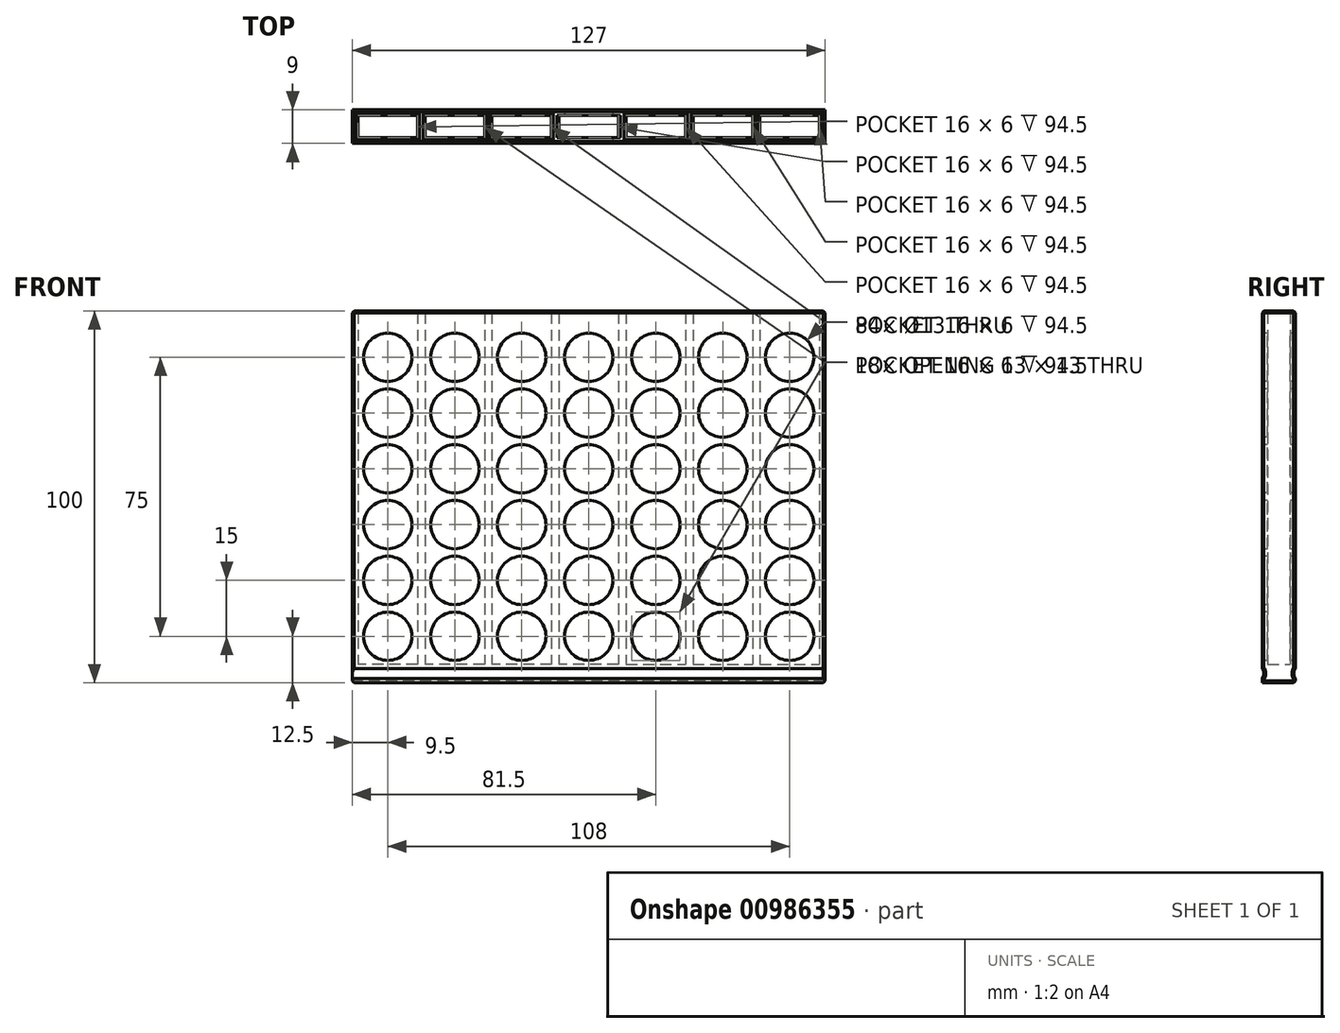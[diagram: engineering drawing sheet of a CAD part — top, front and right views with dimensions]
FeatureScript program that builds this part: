
annotation { "Feature Type Name" : "Feature", "Feature Type Description" : "" }
export const myFeature = defineFeature(function(context is Context, id is Id, definition is map)
    precondition{}
    {
        {
            var Q0;
            Q0=qCreatedBy(makeId("Top.planeOp"),FACE);
            var sketch = newSketch(context, id + "F0", { "sketchPlane" : qUnion([Q0])});
            skLineSegment(sketch, "E0.bottom", {"start": v(63.5, -4.5) * mm, "end": v(-26, -4.5) * mm});
            skLineSegment(sketch, "E0.top", {"start": v(63.5, 4.5) * mm, "end": v(-63.5, 4.5) * mm});
            skLineSegment(sketch, "E0.left", {"start": v(63.5, -4.5) * mm, "end": v(63.5, 4.5) * mm});
            skLineSegment(sketch, "E0.right", {"start": v(-63.5, -4.5) * mm, "end": v(-63.5, 4.5) * mm});
            skPoint(sketch, "E0.middle", {"position": v(0, 0) * mm});
            skLineSegment(sketch, "E1.0", {"start": v(8, 3) * mm, "end": v(-8, 3) * mm});
            skLineSegment(sketch, "E1.1", {"start": v(62, -3) * mm, "end": v(62, 3) * mm});
            skLineSegment(sketch, "E1.2", {"start": v(8, -3) * mm, "end": v(-8, -3) * mm});
            skLineSegment(sketch, "E1.3", {"start": v(-62, -3) * mm, "end": v(-62, 3) * mm});
            skLineSegment(sketch, "E2.left", {"start": v(8, -3) * mm, "end": v(8, 3) * mm, "construction": true});
            skLineSegment(sketch, "E2.right", {"start": v(-8, -3) * mm, "end": v(-8, 3) * mm, "construction": true});
            skLineSegment(sketch, "E3.top", {"start": v(-8, -4.5) * mm, "end": v(-10, -4.5) * mm});
            skLineSegment(sketch, "E3.left", {"start": v(-8, 3) * mm, "end": v(-8, -3) * mm});
            skLineSegment(sketch, "E3.right", {"start": v(-10, 3) * mm, "end": v(-10, -3) * mm});
            skLineSegment(sketch, "E4.top", {"start": v(-10, 4.5) * mm, "end": v(-26, 4.5) * mm, "construction": true});
            skLineSegment(sketch, "E4.left", {"start": v(-10, -3) * mm, "end": v(-10, 3) * mm, "construction": true});
            skLineSegment(sketch, "E4.right", {"start": v(-26, -3) * mm, "end": v(-26, 3) * mm, "construction": true});
            skLineSegment(sketch, "E5.bottom", {"start": v(-26, -4.5) * mm, "end": v(-28, -4.5) * mm});
            skLineSegment(sketch, "E5.top", {"start": v(-26, 4.5) * mm, "end": v(-28, 4.5) * mm});
            skLineSegment(sketch, "E5.left", {"start": v(-26, -3) * mm, "end": v(-26, 3) * mm});
            skLineSegment(sketch, "E5.right", {"start": v(-28, -3) * mm, "end": v(-28, 3) * mm});
            skLineSegment(sketch, "E6.top", {"start": v(-28, 4.5) * mm, "end": v(-44, 4.5) * mm, "construction": true});
            skLineSegment(sketch, "E6.left", {"start": v(-28, -3) * mm, "end": v(-28, 3) * mm, "construction": true});
            skLineSegment(sketch, "E6.right", {"start": v(-44, -3) * mm, "end": v(-44, 3) * mm, "construction": true});
            skLineSegment(sketch, "E7.top", {"start": v(-44, 4.5) * mm, "end": v(-46, 4.5) * mm});
            skLineSegment(sketch, "E7.left", {"start": v(-44, -3) * mm, "end": v(-44, 3) * mm});
            skLineSegment(sketch, "E7.right", {"start": v(-46, -3) * mm, "end": v(-46, 3) * mm});
            skLineSegment(sketch, "E8.top", {"start": v(-46, 4.5) * mm, "end": v(-62, 4.5) * mm, "construction": true});
            skLineSegment(sketch, "E8.left", {"start": v(-46, -3) * mm, "end": v(-46, 3) * mm, "construction": true});
            skLineSegment(sketch, "E8.right", {"start": v(-62, -5) * mm, "end": v(-62, -4.5) * mm, "construction": true});
            skLineSegment(sketch, "E9.trimOffspring", {"start": v(-28, 3) * mm, "end": v(-44, 3) * mm});
            skLineSegment(sketch, "E10.trimOffspring", {"start": v(-46, 3) * mm, "end": v(-62, 3) * mm});
            skLineSegment(sketch, "E11.trimOffspring", {"start": v(-46, -3) * mm, "end": v(-62, -3) * mm});
            skLineSegment(sketch, "E12.trimOffspring", {"start": v(-28, -4.5) * mm, "end": v(-63.5, -4.5) * mm});
            skLineSegment(sketch, "E13.trimOffspring", {"start": v(-28, -3) * mm, "end": v(-44, -3) * mm});
            skLineSegment(sketch, "E14.trimOffspring", {"start": v(-10, 3) * mm, "end": v(-26, 3) * mm});
            skLineSegment(sketch, "E15.trimOffspring", {"start": v(-10, -3) * mm, "end": v(-26, -3) * mm});
            skLineSegment(sketch, "E16", {"start": v(0, 11.85) * mm, "end": v(0, -12.1) * mm, "construction": true});
            skLineSegment(sketch, "E17.MirrorCS", {"start": v(-8, 3) * mm, "end": v(8, 3) * mm});
            skLineSegment(sketch, "E18.MirrorCS", {"start": v(-8, -3) * mm, "end": v(8, -3) * mm});
            skLineSegment(sketch, "E19.MirrorCS", {"start": v(10, -3) * mm, "end": v(10, 3) * mm, "construction": true});
            skLineSegment(sketch, "E20.MirrorCS", {"start": v(10, 3) * mm, "end": v(26, 3) * mm});
            skLineSegment(sketch, "E21.MirrorCS", {"start": v(10, -3) * mm, "end": v(26, -3) * mm});
            skLineSegment(sketch, "E22.MirrorCS", {"start": v(26, -3) * mm, "end": v(26, 3) * mm, "construction": true});
            skLineSegment(sketch, "E23.MirrorCS", {"start": v(28, -3) * mm, "end": v(28, 3) * mm, "construction": true});
            skLineSegment(sketch, "E24.MirrorCS", {"start": v(28, 3) * mm, "end": v(44, 3) * mm});
            skLineSegment(sketch, "E25.MirrorCS", {"start": v(28, -3) * mm, "end": v(44, -3) * mm});
            skLineSegment(sketch, "E26.MirrorCS", {"start": v(46, -3) * mm, "end": v(62, -3) * mm});
            skLineSegment(sketch, "E27.MirrorCS", {"start": v(46, 3) * mm, "end": v(62, 3) * mm});
            skLineSegment(sketch, "E28.MirrorCS", {"start": v(46, -3) * mm, "end": v(46, 3) * mm, "construction": true});
            skLineSegment(sketch, "E29.MirrorCS", {"start": v(44, -3) * mm, "end": v(44, 3) * mm, "construction": true});
            skLineSegment(sketch, "E30", {"start": v(10, 3) * mm, "end": v(10, -3) * mm});
            skLineSegment(sketch, "E31", {"start": v(26, 3) * mm, "end": v(26, -3) * mm});
            skLineSegment(sketch, "E32", {"start": v(28, 3) * mm, "end": v(28, -3) * mm});
            skLineSegment(sketch, "E33", {"start": v(44, 3) * mm, "end": v(44, -3) * mm});
            skLineSegment(sketch, "E34", {"start": v(46, 3) * mm, "end": v(46, -3) * mm});
            skLineSegment(sketch, "E35", {"start": v(8, 3) * mm, "end": v(8, -3) * mm});
            skPoint(sketch, "E36.orphan", {"position": v(-8, -6) * mm});
            skPoint(sketch, "E2.bottom.start.orphan", {"position": v(8, -6) * mm});
            skPoint(sketch, "E37.orphan", {"position": v(8, 6) * mm});
            skPoint(sketch, "E3.bottom.start.orphan", {"position": v(-8, 6) * mm});
            skSolve(sketch);
        }
        {
            var Q0;
            {var subQ6=sQuery(id+"F0.wireOp",EDGE,"E0.left");Q0=makeQuery(id+"F0.imprint","IMPRINT",FACE,{"disambiguationData":[TD([[makeQuery(id+"F0.imprint","IMPRINT",EDGE,{"derivedFrom":subQ6}),1.0]])]});}
            extrude(context, id + "F1", {"entities" : qUnion([Q0]), "depth" : 95 * mm, "offsetDistance" : 25 * mm});
        }
        {
            var Q0;
            Q0=makeQuery(id+"F0.imprint","IMPRINT",FACE,{"disambiguationData":[TD([[makeQuery(id+"F0.imprint","IMPRINT",EDGE,{"derivedFrom":sQuery(id+"F0.wireOp",EDGE,"E1.3")}),-1.0]])]});
            var Q1;
            Q1=makeQuery(id+"F0.imprint","IMPRINT",FACE,{"disambiguationData":[TD([[makeQuery(id+"F0.imprint","IMPRINT",EDGE,{"derivedFrom":sQuery(id+"F0.wireOp",EDGE,"E5.right")}),1.0]])]});
            var Q2;
            {var subQ6=sQuery(id+"F0.wireOp",EDGE,"E0.left");Q2=makeQuery(id+"F0.imprint","IMPRINT",FACE,{"disambiguationData":[TD([[makeQuery(id+"F0.imprint","IMPRINT",EDGE,{"derivedFrom":subQ6}),1.0]])]});}
            var Q3;
            Q3=makeQuery(id+"F0.imprint","IMPRINT",FACE,{"disambiguationData":[TD([[makeQuery(id+"F0.imprint","IMPRINT",EDGE,{"derivedFrom":sQuery(id+"F0.wireOp",EDGE,"E3.right")}),-1.0]])]});
            var Q4;
            Q4=makeQuery(id+"F0.imprint","IMPRINT",FACE,{"disambiguationData":[TD([[makeQuery(id+"F0.imprint","IMPRINT",EDGE,{"derivedFrom":sQuery(id+"F0.wireOp",EDGE,"E3.left")}),1.0]])]});
            var Q5;
            Q5=makeQuery(id+"F0.imprint","IMPRINT",FACE,{"disambiguationData":[TD([[makeQuery(id+"F0.imprint","IMPRINT",EDGE,{"derivedFrom":sQuery(id+"F0.wireOp",EDGE,"E20.MirrorCS")}),-1.0]])]});
            var Q6;
            Q6=makeQuery(id+"F0.imprint","IMPRINT",FACE,{"disambiguationData":[TD([[makeQuery(id+"F0.imprint","IMPRINT",EDGE,{"derivedFrom":sQuery(id+"F0.wireOp",EDGE,"E24.MirrorCS")}),-1.0]])]});
            var Q7;
            Q7=makeQuery(id+"F0.imprint","IMPRINT",FACE,{"disambiguationData":[TD([[makeQuery(id+"F0.imprint","IMPRINT",EDGE,{"derivedFrom":sQuery(id+"F0.wireOp",EDGE,"E26.MirrorCS")}),1.0]])]});
            extrude(context, id + "F2", {"entities" : qUnion([Q0, Q1, Q2, Q3, Q4, Q5, Q6, Q7]), "operationType" : NewBodyOperationType.ADD, "oppositeDirection" : true, "depth" : 5 * mm, "offsetDistance" : 25 * mm});
        }
        {
            var Q0;
            Q0=makeQuery(id+"F1.opExtrude","CAP_FACE",FACE,{"disambiguationData":[OSD([sQuery(id+"F0.wireOp",EDGE,"E0.bottom"),sQuery(id+"F0.wireOp",EDGE,"E0.top"),sQuery(id+"F0.wireOp",EDGE,"E0.left"),sQuery(id+"F0.wireOp",EDGE,"E0.right"),sQuery(id+"F0.wireOp",EDGE,"E1.3"),sQuery(id+"F0.wireOp",EDGE,"E3.bottom"),sQuery(id+"F0.wireOp",EDGE,"E3.top"),sQuery(id+"F0.wireOp",EDGE,"E3.left"),sQuery(id+"F0.wireOp",EDGE,"E3.right"),sQuery(id+"F0.wireOp",EDGE,"E5.bottom"),sQuery(id+"F0.wireOp",EDGE,"E5.top"),sQuery(id+"F0.wireOp",EDGE,"E5.left"),sQuery(id+"F0.wireOp",EDGE,"E5.right"),sQuery(id+"F0.wireOp",EDGE,"E7.top"),sQuery(id+"F0.wireOp",EDGE,"E7.left"),sQuery(id+"F0.wireOp",EDGE,"E7.right"),sQuery(id+"F0.wireOp",EDGE,"E9.trimOffspring"),sQuery(id+"F0.wireOp",EDGE,"E10.trimOffspring"),sQuery(id+"F0.wireOp",EDGE,"E11.trimOffspring"),sQuery(id+"F0.wireOp",EDGE,"E12.trimOffspring"),sQuery(id+"F0.wireOp",EDGE,"E13.trimOffspring"),sQuery(id+"F0.wireOp",EDGE,"E14.trimOffspring"),sQuery(id+"F0.wireOp",EDGE,"E15.trimOffspring"),sQuery(id+"F0.wireOp",EDGE,"E17.MirrorCS"),sQuery(id+"F0.wireOp",EDGE,"E18.MirrorCS"),sQuery(id+"F0.wireOp",EDGE,"E20.MirrorCS"),sQuery(id+"F0.wireOp",EDGE,"E21.MirrorCS"),sQuery(id+"F0.wireOp",EDGE,"E24.MirrorCS"),sQuery(id+"F0.wireOp",EDGE,"E25.MirrorCS"),sQuery(id+"F0.wireOp",EDGE,"E26.MirrorCS"),sQuery(id+"F0.wireOp",EDGE,"E27.MirrorCS"),sQuery(id+"F0.wireOp",EDGE,"E1.1"),sQuery(id+"F0.wireOp",EDGE,"E30"),sQuery(id+"F0.wireOp",EDGE,"E31"),sQuery(id+"F0.wireOp",EDGE,"E32"),sQuery(id+"F0.wireOp",EDGE,"E33"),sQuery(id+"F0.wireOp",EDGE,"E34"),sQuery(id+"F0.wireOp",EDGE,"E35")])],"isStart":false});
            var sketch = newSketch(context, id + "F3", { "sketchPlane" : qUnion([Q0])});
            skLineSegment(sketch, "E38", {"start": v(-18, -3) * mm, "end": v(-18, -4.5) * mm, "construction": true});
            skLineSegment(sketch, "E39", {"start": v(-36, -3) * mm, "end": v(-36, -4.5) * mm, "construction": true});
            skLineSegment(sketch, "E40", {"start": v(-54, -3) * mm, "end": v(-54, -4.5) * mm, "construction": true});
            skLineSegment(sketch, "E41", {"start": v(0, -3) * mm, "end": v(0, -4.5) * mm, "construction": true});
            skSolve(sketch);
        }
        {
            var Q0;
            {var subQ0=sQuery(id+"F0.wireOp",EDGE,"E12.trimOffspring");var subQ1=sQuery(id+"F0.wireOp",EDGE,"E5.bottom");var subQ2=sQuery(id+"F0.wireOp",EDGE,"E3.top");var subQ3=sQuery(id+"F0.wireOp",EDGE,"E0.bottom");Q0=makeQuery(id+"F2.boolean.opBoolean","MERGE",FACE,{"derivedFrom":[makeQuery(id+"F1.opExtrude","SWEPT_FACE",FACE,{"disambiguationData":[OSD([subQ3,subQ2,subQ1,subQ0])]}),makeQuery(id+"F2.opExtrude","SWEPT_FACE",FACE,{"disambiguationData":[OSD([subQ3,subQ2,subQ1,subQ0])]})]});}
            var sketch = newSketch(context, id + "F4", { "sketchPlane" : qUnion([Q0])});
            skLineSegment(sketch, "E42", {"start": v(-54, 95) * mm, "end": v(-54, -5) * mm, "construction": true});
            skLineSegment(sketch, "E43", {"start": v(-36, 95) * mm, "end": v(-36, -5) * mm, "construction": true});
            skLineSegment(sketch, "E44", {"start": v(-18, 95) * mm, "end": v(-18, -5) * mm, "construction": true});
            skLineSegment(sketch, "E45", {"start": v(0, 95) * mm, "end": v(0, -5) * mm, "construction": true});
            skLineSegment(sketch, "E46", {"start": v(-63.5, 0) * mm, "end": v(63.5, 0) * mm, "construction": true});
            skCircle(sketch, "E47", {"center": v(-54, 7.5) * mm, "radius": 7.5 * mm, "construction": true});
            skCircle(sketch, "E48", {"center": v(-54, 22.5) * mm, "radius": 7.5 * mm, "construction": true});
            skCircle(sketch, "E49", {"center": v(-54, 37.5) * mm, "radius": 7.5 * mm, "construction": true});
            skCircle(sketch, "E50", {"center": v(-54, 52.5) * mm, "radius": 7.5 * mm, "construction": true});
            skCircle(sketch, "E51", {"center": v(-54, 67.5) * mm, "radius": 7.5 * mm, "construction": true});
            skCircle(sketch, "E52", {"center": v(-54, 82.5) * mm, "radius": 7.5 * mm, "construction": true});
            skCircle(sketch, "E53", {"center": v(-54, 82.5) * mm, "radius": 6.5 * mm});
            skCircle(sketch, "E54", {"center": v(-54, 67.5) * mm, "radius": 6.5 * mm});
            skCircle(sketch, "E55", {"center": v(-54, 52.5) * mm, "radius": 6.5 * mm});
            skCircle(sketch, "E56", {"center": v(-54, 37.5) * mm, "radius": 6.5 * mm});
            skCircle(sketch, "E57", {"center": v(-54, 22.5) * mm, "radius": 6.5 * mm});
            skCircle(sketch, "E58", {"center": v(-54, 7.5) * mm, "radius": 6.5 * mm});
            skCircle(sketch, "E59.MirrorC", {"center": v(54, 82.5) * mm, "radius": 6.5 * mm});
            skCircle(sketch, "E60.MirrorC", {"center": v(54, 67.5) * mm, "radius": 6.5 * mm});
            skCircle(sketch, "E61.MirrorC", {"center": v(54, 52.5) * mm, "radius": 6.5 * mm});
            skCircle(sketch, "E62.MirrorC", {"center": v(54, 37.5) * mm, "radius": 6.5 * mm});
            skCircle(sketch, "E63.MirrorC", {"center": v(54, 22.5) * mm, "radius": 6.5 * mm});
            skCircle(sketch, "E64.MirrorC", {"center": v(54, 7.5) * mm, "radius": 6.5 * mm});
            skCircle(sketch, "E65.MirrorC", {"center": v(18, 82.5) * mm, "radius": 6.5 * mm});
            skCircle(sketch, "E66.MirrorC", {"center": v(18, 67.5) * mm, "radius": 6.5 * mm});
            skCircle(sketch, "E67.MirrorC", {"center": v(18, 52.5) * mm, "radius": 6.5 * mm});
            skCircle(sketch, "E68.MirrorC", {"center": v(18, 37.5) * mm, "radius": 6.5 * mm});
            skCircle(sketch, "E69.MirrorC", {"center": v(18, 22.5) * mm, "radius": 6.5 * mm});
            skCircle(sketch, "E70.MirrorC", {"center": v(18, 7.5) * mm, "radius": 6.5 * mm});
            skCircle(sketch, "E71.MirrorC", {"center": v(-18, 82.5) * mm, "radius": 6.5 * mm});
            skCircle(sketch, "E72.MirrorC", {"center": v(-18, 67.5) * mm, "radius": 6.5 * mm});
            skCircle(sketch, "E73.MirrorC", {"center": v(-18, 52.5) * mm, "radius": 6.5 * mm});
            skCircle(sketch, "E74.MirrorC", {"center": v(-18, 37.5) * mm, "radius": 6.5 * mm});
            skCircle(sketch, "E75.MirrorC", {"center": v(-18, 22.5) * mm, "radius": 6.5 * mm});
            skCircle(sketch, "E76.MirrorC", {"center": v(-18, 7.5) * mm, "radius": 6.5 * mm});
            skLineSegment(sketch, "E77", {"start": v(-45, 95) * mm, "end": v(-45, 0) * mm, "construction": true});
            skCircle(sketch, "E78.MirrorC", {"center": v(-36, 82.5) * mm, "radius": 6.5 * mm});
            skCircle(sketch, "E79.MirrorC", {"center": v(-36, 67.5) * mm, "radius": 6.5 * mm});
            skCircle(sketch, "E80.MirrorC", {"center": v(-36, 52.5) * mm, "radius": 6.5 * mm});
            skCircle(sketch, "E81.MirrorC", {"center": v(-36, 37.5) * mm, "radius": 6.5 * mm});
            skCircle(sketch, "E82.MirrorC", {"center": v(-36, 22.5) * mm, "radius": 6.5 * mm});
            skCircle(sketch, "E83.MirrorC", {"center": v(-36, 7.5) * mm, "radius": 6.5 * mm});
            skCircle(sketch, "E84.MirrorC", {"center": v(0, 82.5) * mm, "radius": 6.5 * mm});
            skCircle(sketch, "E85.MirrorC", {"center": v(0, 67.5) * mm, "radius": 6.5 * mm});
            skCircle(sketch, "E86.MirrorC", {"center": v(0, 52.5) * mm, "radius": 6.5 * mm});
            skCircle(sketch, "E87.MirrorC", {"center": v(0, 37.5) * mm, "radius": 6.5 * mm});
            skCircle(sketch, "E88.MirrorC", {"center": v(0, 22.5) * mm, "radius": 6.5 * mm});
            skCircle(sketch, "E89.MirrorC", {"center": v(0, 7.5) * mm, "radius": 6.5 * mm});
            skCircle(sketch, "E90.MirrorC", {"center": v(36, 82.5) * mm, "radius": 6.5 * mm});
            skCircle(sketch, "E91.MirrorC", {"center": v(36, 67.5) * mm, "radius": 6.5 * mm});
            skCircle(sketch, "E92.MirrorC", {"center": v(36, 52.5) * mm, "radius": 6.5 * mm});
            skCircle(sketch, "E93.MirrorC", {"center": v(36, 37.5) * mm, "radius": 6.5 * mm});
            skCircle(sketch, "E94.MirrorC", {"center": v(36, 22.5) * mm, "radius": 6.5 * mm});
            skCircle(sketch, "E95.MirrorC", {"center": v(36, 7.5) * mm, "radius": 6.5 * mm});
            skSolve(sketch);
        }
        {
            var Q0;
            Q0 = qSketchRegion(id + "F4", true);
            extrude(context, id + "F5", {"entities" : qUnion([Q0]), "operationType" : NewBodyOperationType.ADD, "depth" : 25 * mm, "offsetDistance" : 25 * mm});
        }
        {
            var Q0;
            Q0=makeQuery(id+"F5.opExtrude","CAP_FACE",FACE,{"disambiguationData":[OSD([sQuery(id+"F4.wireOp",EDGE,"E53")])],"isStart":false});
            var Q1;
            Q1=makeQuery(id+"F5.opExtrude","CAP_FACE",FACE,{"disambiguationData":[OSD([sQuery(id+"F4.wireOp",EDGE,"E78.MirrorC")])],"isStart":false});
            var Q2;
            Q2=makeQuery(id+"F5.opExtrude","CAP_FACE",FACE,{"disambiguationData":[OSD([sQuery(id+"F4.wireOp",EDGE,"E71.MirrorC")])],"isStart":false});
            var Q3;
            Q3=makeQuery(id+"F5.opExtrude","CAP_FACE",FACE,{"disambiguationData":[OSD([sQuery(id+"F4.wireOp",EDGE,"E84.MirrorC")])],"isStart":false});
            var Q4;
            Q4=makeQuery(id+"F5.opExtrude","CAP_FACE",FACE,{"disambiguationData":[OSD([sQuery(id+"F4.wireOp",EDGE,"E65.MirrorC")])],"isStart":false});
            var Q5;
            Q5=makeQuery(id+"F5.opExtrude","CAP_FACE",FACE,{"disambiguationData":[OSD([sQuery(id+"F4.wireOp",EDGE,"E90.MirrorC")])],"isStart":false});
            var Q6;
            Q6=makeQuery(id+"F5.opExtrude","CAP_FACE",FACE,{"disambiguationData":[OSD([sQuery(id+"F4.wireOp",EDGE,"E59.MirrorC")])],"isStart":false});
            var Q7;
            Q7=makeQuery(id+"F5.opExtrude","CAP_FACE",FACE,{"disambiguationData":[OSD([sQuery(id+"F4.wireOp",EDGE,"E60.MirrorC")])],"isStart":false});
            var Q8;
            Q8=makeQuery(id+"F5.opExtrude","CAP_FACE",FACE,{"disambiguationData":[OSD([sQuery(id+"F4.wireOp",EDGE,"E61.MirrorC")])],"isStart":false});
            var Q9;
            Q9=makeQuery(id+"F5.opExtrude","CAP_FACE",FACE,{"disambiguationData":[OSD([sQuery(id+"F4.wireOp",EDGE,"E62.MirrorC")])],"isStart":false});
            var Q10;
            Q10=makeQuery(id+"F5.opExtrude","CAP_FACE",FACE,{"disambiguationData":[OSD([sQuery(id+"F4.wireOp",EDGE,"E63.MirrorC")])],"isStart":false});
            var Q11;
            Q11=makeQuery(id+"F5.opExtrude","CAP_FACE",FACE,{"disambiguationData":[OSD([sQuery(id+"F4.wireOp",EDGE,"E64.MirrorC")])],"isStart":false});
            var Q12;
            Q12=makeQuery(id+"F5.opExtrude","CAP_FACE",FACE,{"disambiguationData":[OSD([sQuery(id+"F4.wireOp",EDGE,"E95.MirrorC")])],"isStart":false});
            var Q13;
            Q13=makeQuery(id+"F5.opExtrude","CAP_FACE",FACE,{"disambiguationData":[OSD([sQuery(id+"F4.wireOp",EDGE,"E94.MirrorC")])],"isStart":false});
            var Q14;
            Q14=makeQuery(id+"F5.opExtrude","CAP_FACE",FACE,{"disambiguationData":[OSD([sQuery(id+"F4.wireOp",EDGE,"E93.MirrorC")])],"isStart":false});
            var Q15;
            Q15=makeQuery(id+"F5.opExtrude","CAP_FACE",FACE,{"disambiguationData":[OSD([sQuery(id+"F4.wireOp",EDGE,"E92.MirrorC")])],"isStart":false});
            var Q16;
            Q16=makeQuery(id+"F5.opExtrude","CAP_FACE",FACE,{"disambiguationData":[OSD([sQuery(id+"F4.wireOp",EDGE,"E91.MirrorC")])],"isStart":false});
            var Q17;
            Q17=makeQuery(id+"F5.opExtrude","CAP_FACE",FACE,{"disambiguationData":[OSD([sQuery(id+"F4.wireOp",EDGE,"E66.MirrorC")])],"isStart":false});
            var Q18;
            Q18=makeQuery(id+"F5.opExtrude","CAP_FACE",FACE,{"disambiguationData":[OSD([sQuery(id+"F4.wireOp",EDGE,"E67.MirrorC")])],"isStart":false});
            var Q19;
            Q19=makeQuery(id+"F5.opExtrude","CAP_FACE",FACE,{"disambiguationData":[OSD([sQuery(id+"F4.wireOp",EDGE,"E68.MirrorC")])],"isStart":false});
            var Q20;
            Q20=makeQuery(id+"F5.opExtrude","CAP_FACE",FACE,{"disambiguationData":[OSD([sQuery(id+"F4.wireOp",EDGE,"E69.MirrorC")])],"isStart":false});
            var Q21;
            Q21=makeQuery(id+"F5.opExtrude","CAP_FACE",FACE,{"disambiguationData":[OSD([sQuery(id+"F4.wireOp",EDGE,"E70.MirrorC")])],"isStart":false});
            var Q22;
            Q22=makeQuery(id+"F5.opExtrude","CAP_FACE",FACE,{"disambiguationData":[OSD([sQuery(id+"F4.wireOp",EDGE,"E89.MirrorC")])],"isStart":false});
            var Q23;
            Q23=makeQuery(id+"F5.opExtrude","CAP_FACE",FACE,{"disambiguationData":[OSD([sQuery(id+"F4.wireOp",EDGE,"E88.MirrorC")])],"isStart":false});
            var Q24;
            Q24=makeQuery(id+"F5.opExtrude","CAP_FACE",FACE,{"disambiguationData":[OSD([sQuery(id+"F4.wireOp",EDGE,"E87.MirrorC")])],"isStart":false});
            var Q25;
            Q25=makeQuery(id+"F5.opExtrude","CAP_FACE",FACE,{"disambiguationData":[OSD([sQuery(id+"F4.wireOp",EDGE,"E86.MirrorC")])],"isStart":false});
            var Q26;
            Q26=makeQuery(id+"F5.opExtrude","CAP_FACE",FACE,{"disambiguationData":[OSD([sQuery(id+"F4.wireOp",EDGE,"E85.MirrorC")])],"isStart":false});
            var Q27;
            Q27=makeQuery(id+"F5.opExtrude","CAP_FACE",FACE,{"disambiguationData":[OSD([sQuery(id+"F4.wireOp",EDGE,"E72.MirrorC")])],"isStart":false});
            var Q28;
            Q28=makeQuery(id+"F5.opExtrude","CAP_FACE",FACE,{"disambiguationData":[OSD([sQuery(id+"F4.wireOp",EDGE,"E73.MirrorC")])],"isStart":false});
            var Q29;
            Q29=makeQuery(id+"F5.opExtrude","CAP_FACE",FACE,{"disambiguationData":[OSD([sQuery(id+"F4.wireOp",EDGE,"E74.MirrorC")])],"isStart":false});
            var Q30;
            Q30=makeQuery(id+"F5.opExtrude","CAP_FACE",FACE,{"disambiguationData":[OSD([sQuery(id+"F4.wireOp",EDGE,"E75.MirrorC")])],"isStart":false});
            var Q31;
            Q31=makeQuery(id+"F5.opExtrude","CAP_FACE",FACE,{"disambiguationData":[OSD([sQuery(id+"F4.wireOp",EDGE,"E76.MirrorC")])],"isStart":false});
            var Q32;
            Q32=makeQuery(id+"F5.opExtrude","CAP_FACE",FACE,{"disambiguationData":[OSD([sQuery(id+"F4.wireOp",EDGE,"E83.MirrorC")])],"isStart":false});
            var Q33;
            Q33=makeQuery(id+"F5.opExtrude","CAP_FACE",FACE,{"disambiguationData":[OSD([sQuery(id+"F4.wireOp",EDGE,"E82.MirrorC")])],"isStart":false});
            var Q34;
            Q34=makeQuery(id+"F5.opExtrude","CAP_FACE",FACE,{"disambiguationData":[OSD([sQuery(id+"F4.wireOp",EDGE,"E81.MirrorC")])],"isStart":false});
            var Q35;
            Q35=makeQuery(id+"F5.opExtrude","CAP_FACE",FACE,{"disambiguationData":[OSD([sQuery(id+"F4.wireOp",EDGE,"E80.MirrorC")])],"isStart":false});
            var Q36;
            Q36=makeQuery(id+"F5.opExtrude","CAP_FACE",FACE,{"disambiguationData":[OSD([sQuery(id+"F4.wireOp",EDGE,"E79.MirrorC")])],"isStart":false});
            var Q37;
            Q37=makeQuery(id+"F5.opExtrude","CAP_FACE",FACE,{"disambiguationData":[OSD([sQuery(id+"F4.wireOp",EDGE,"E54")])],"isStart":false});
            var Q38;
            Q38=makeQuery(id+"F5.opExtrude","CAP_FACE",FACE,{"disambiguationData":[OSD([sQuery(id+"F4.wireOp",EDGE,"E55")])],"isStart":false});
            var Q39;
            Q39=makeQuery(id+"F5.opExtrude","CAP_FACE",FACE,{"disambiguationData":[OSD([sQuery(id+"F4.wireOp",EDGE,"E56")])],"isStart":false});
            var Q40;
            Q40=makeQuery(id+"F5.opExtrude","CAP_FACE",FACE,{"disambiguationData":[OSD([sQuery(id+"F4.wireOp",EDGE,"E57")])],"isStart":false});
            var Q41;
            Q41=makeQuery(id+"F5.opExtrude","CAP_FACE",FACE,{"disambiguationData":[OSD([sQuery(id+"F4.wireOp",EDGE,"E58")])],"isStart":false});
            extrude(context, id + "F6", {"entities" : qUnion([Q0, Q1, Q2, Q3, Q4, Q5, Q6, Q7, Q8, Q9, Q10, Q11, Q12, Q13, Q14, Q15, Q16, Q17, Q18, Q19, Q20, Q21, Q22, Q23, Q24, Q25, Q26, Q27, Q28, Q29, Q30, Q31, Q32, Q33, Q34, Q35, Q36, Q37, Q38, Q39, Q40, Q41]), "operationType" : NewBodyOperationType.REMOVE, "endBound" : BoundingType.THROUGH_ALL, "oppositeDirection" : true, "depth" : 25 * mm, "offsetDistance" : 25 * mm});
        }
        {
            var Q0;
            {var subQ0=sQuery(id+"F0.wireOp",EDGE,"E0.right");Q0=makeQuery(id+"F2.boolean.opBoolean","MERGE",FACE,{"derivedFrom":[makeQuery(id+"F1.opExtrude","SWEPT_FACE",FACE,{"disambiguationData":[OSD([subQ0])]}),makeQuery(id+"F2.opExtrude","SWEPT_FACE",FACE,{"disambiguationData":[OSD([subQ0])]})]});}
            var sketch = newSketch(context, id + "F7", { "sketchPlane" : qUnion([Q0])});
            skLineSegment(sketch, "E96", {"start": v(0, 0) * mm, "end": v(0, -7.08) * mm, "construction": true});
            skLineSegment(sketch, "E97", {"start": v(-6.2, -2.5) * mm, "end": v(6.74, -2.5) * mm, "construction": true});
            skCircle(sketch, "E98", {"center": v(-6, -2.5) * mm, "radius": 2 * mm});
            skCircle(sketch, "E99.MirrorC", {"center": v(6, -2.5) * mm, "radius": 2 * mm});
            skSolve(sketch);
        }
        {
            var Q0;
            Q0 = qSketchRegion(id + "F7", true);
            extrude(context, id + "F8", {"entities" : qUnion([Q0]), "operationType" : NewBodyOperationType.REMOVE, "endBound" : BoundingType.THROUGH_ALL, "oppositeDirection" : true, "depth" : 25 * mm, "offsetDistance" : 25 * mm});
        }
        {
            var Q0;
            {var subQ0=sQuery(id+"F0.wireOp",EDGE,"E7.top");var subQ1=sQuery(id+"F0.wireOp",EDGE,"E5.top");var subQ2=sQuery(id+"F0.wireOp",EDGE,"E0.top");var subQ3=sQuery(id+"F0.wireOp",EDGE,"E0.right");Q0=makeQuery(id+"F8.boolean.opBoolean","SPLIT",EDGE,{"disambiguationData":[TD([makeQuery(id+"F1.opExtrude","CAP_FACE",FACE,{"disambiguationData":[OSD([sQuery(id+"F0.wireOp",EDGE,"E0.bottom"),subQ2,sQuery(id+"F0.wireOp",EDGE,"E0.left"),subQ3,sQuery(id+"F0.wireOp",EDGE,"E1.3"),sQuery(id+"F0.wireOp",EDGE,"E3.top"),sQuery(id+"F0.wireOp",EDGE,"E3.left"),sQuery(id+"F0.wireOp",EDGE,"E3.right"),sQuery(id+"F0.wireOp",EDGE,"E5.bottom"),subQ1,sQuery(id+"F0.wireOp",EDGE,"E5.left"),sQuery(id+"F0.wireOp",EDGE,"E5.right"),subQ0,sQuery(id+"F0.wireOp",EDGE,"E7.left"),sQuery(id+"F0.wireOp",EDGE,"E7.right"),sQuery(id+"F0.wireOp",EDGE,"E9.trimOffspring"),sQuery(id+"F0.wireOp",EDGE,"E10.trimOffspring"),sQuery(id+"F0.wireOp",EDGE,"E11.trimOffspring"),sQuery(id+"F0.wireOp",EDGE,"E12.trimOffspring"),sQuery(id+"F0.wireOp",EDGE,"E13.trimOffspring"),sQuery(id+"F0.wireOp",EDGE,"E14.trimOffspring"),sQuery(id+"F0.wireOp",EDGE,"E15.trimOffspring"),sQuery(id+"F0.wireOp",EDGE,"E17.MirrorCS"),sQuery(id+"F0.wireOp",EDGE,"E18.MirrorCS"),sQuery(id+"F0.wireOp",EDGE,"E20.MirrorCS"),sQuery(id+"F0.wireOp",EDGE,"E21.MirrorCS"),sQuery(id+"F0.wireOp",EDGE,"E24.MirrorCS"),sQuery(id+"F0.wireOp",EDGE,"E25.MirrorCS"),sQuery(id+"F0.wireOp",EDGE,"E26.MirrorCS"),sQuery(id+"F0.wireOp",EDGE,"E27.MirrorCS"),sQuery(id+"F0.wireOp",EDGE,"E1.1"),sQuery(id+"F0.wireOp",EDGE,"E30"),sQuery(id+"F0.wireOp",EDGE,"E31"),sQuery(id+"F0.wireOp",EDGE,"E32"),sQuery(id+"F0.wireOp",EDGE,"E33"),sQuery(id+"F0.wireOp",EDGE,"E34"),sQuery(id+"F0.wireOp",EDGE,"E35")])],"isStart":false})])],"derivedFrom":makeQuery(id+"F2.boolean.opBoolean","MERGE",EDGE,{"derivedFrom":[makeQuery(id+"F1.opExtrude","SWEPT_EDGE",EDGE,{"disambiguationData":[OSD([subQ2,subQ3])]}),makeQuery(id+"F2.opExtrude","SWEPT_EDGE",EDGE,{"disambiguationData":[OSD([subQ2,subQ3])]})]})});}
            var Q1;
            {var subQ0=sQuery(id+"F0.wireOp",EDGE,"E12.trimOffspring");var subQ1=sQuery(id+"F0.wireOp",EDGE,"E5.bottom");var subQ2=sQuery(id+"F0.wireOp",EDGE,"E3.top");var subQ3=sQuery(id+"F0.wireOp",EDGE,"E0.bottom");var subQ4=sQuery(id+"F0.wireOp",EDGE,"E0.right");Q1=makeQuery(id+"F8.boolean.opBoolean","SPLIT",EDGE,{"disambiguationData":[TD([makeQuery(id+"F1.opExtrude","CAP_FACE",FACE,{"disambiguationData":[OSD([subQ3,sQuery(id+"F0.wireOp",EDGE,"E0.top"),sQuery(id+"F0.wireOp",EDGE,"E0.left"),subQ4,sQuery(id+"F0.wireOp",EDGE,"E1.3"),subQ2,sQuery(id+"F0.wireOp",EDGE,"E3.left"),sQuery(id+"F0.wireOp",EDGE,"E3.right"),subQ1,sQuery(id+"F0.wireOp",EDGE,"E5.top"),sQuery(id+"F0.wireOp",EDGE,"E5.left"),sQuery(id+"F0.wireOp",EDGE,"E5.right"),sQuery(id+"F0.wireOp",EDGE,"E7.top"),sQuery(id+"F0.wireOp",EDGE,"E7.left"),sQuery(id+"F0.wireOp",EDGE,"E7.right"),sQuery(id+"F0.wireOp",EDGE,"E9.trimOffspring"),sQuery(id+"F0.wireOp",EDGE,"E10.trimOffspring"),sQuery(id+"F0.wireOp",EDGE,"E11.trimOffspring"),subQ0,sQuery(id+"F0.wireOp",EDGE,"E13.trimOffspring"),sQuery(id+"F0.wireOp",EDGE,"E14.trimOffspring"),sQuery(id+"F0.wireOp",EDGE,"E15.trimOffspring"),sQuery(id+"F0.wireOp",EDGE,"E17.MirrorCS"),sQuery(id+"F0.wireOp",EDGE,"E18.MirrorCS"),sQuery(id+"F0.wireOp",EDGE,"E20.MirrorCS"),sQuery(id+"F0.wireOp",EDGE,"E21.MirrorCS"),sQuery(id+"F0.wireOp",EDGE,"E24.MirrorCS"),sQuery(id+"F0.wireOp",EDGE,"E25.MirrorCS"),sQuery(id+"F0.wireOp",EDGE,"E26.MirrorCS"),sQuery(id+"F0.wireOp",EDGE,"E27.MirrorCS"),sQuery(id+"F0.wireOp",EDGE,"E1.1"),sQuery(id+"F0.wireOp",EDGE,"E30"),sQuery(id+"F0.wireOp",EDGE,"E31"),sQuery(id+"F0.wireOp",EDGE,"E32"),sQuery(id+"F0.wireOp",EDGE,"E33"),sQuery(id+"F0.wireOp",EDGE,"E34"),sQuery(id+"F0.wireOp",EDGE,"E35")])],"isStart":false})])],"derivedFrom":makeQuery(id+"F2.boolean.opBoolean","MERGE",EDGE,{"derivedFrom":[makeQuery(id+"F1.opExtrude","SWEPT_EDGE",EDGE,{"disambiguationData":[OSD([subQ4,subQ0])]}),makeQuery(id+"F2.opExtrude","SWEPT_EDGE",EDGE,{"disambiguationData":[OSD([subQ4,subQ0])]})]})});}
            var Q2;
            Q2=makeQuery(id+"F2.opExtrude","CAP_EDGE",EDGE,{"disambiguationData":[OSD([sQuery(id+"F0.wireOp",EDGE,"E0.top"),sQuery(id+"F0.wireOp",EDGE,"E5.top"),sQuery(id+"F0.wireOp",EDGE,"E7.top")])],"isStart":false});
            var Q3;
            Q3=makeQuery(id+"F2.opExtrude","CAP_EDGE",EDGE,{"disambiguationData":[OSD([sQuery(id+"F0.wireOp",EDGE,"E0.right")])],"isStart":false});
            var Q4;
            Q4=makeQuery(id+"F8.boolean.opBoolean","COPY",EDGE,{"derivedFrom":makeQuery(id+"F8.opExtrude","CAP_EDGE",EDGE,{"disambiguationData":[OSD([sQuery(id+"F7.wireOp",EDGE,"E98")])],"isStart":true})});
            var Q5;
            Q5=makeQuery(id+"F1.opExtrude","CAP_EDGE",EDGE,{"disambiguationData":[OSD([sQuery(id+"F0.wireOp",EDGE,"E0.top"),sQuery(id+"F0.wireOp",EDGE,"E5.top"),sQuery(id+"F0.wireOp",EDGE,"E7.top")])],"isStart":false});
            var Q6;
            Q6=makeQuery(id+"F1.opExtrude","CAP_EDGE",EDGE,{"disambiguationData":[OSD([sQuery(id+"F0.wireOp",EDGE,"E0.right")])],"isStart":false});
            var Q7;
            Q7=makeQuery(id+"F1.opExtrude","CAP_EDGE",EDGE,{"disambiguationData":[OSD([sQuery(id+"F0.wireOp",EDGE,"E0.bottom"),sQuery(id+"F0.wireOp",EDGE,"E3.top"),sQuery(id+"F0.wireOp",EDGE,"E5.bottom"),sQuery(id+"F0.wireOp",EDGE,"E12.trimOffspring")])],"isStart":false});
            var Q8;
            Q8=makeQuery(id+"F1.opExtrude","CAP_EDGE",EDGE,{"disambiguationData":[OSD([sQuery(id+"F0.wireOp",EDGE,"E0.left")])],"isStart":false});
            var Q9;
            Q9=makeQuery(id+"F2.opExtrude","CAP_EDGE",EDGE,{"disambiguationData":[OSD([sQuery(id+"F0.wireOp",EDGE,"E0.left")])],"isStart":false});
            var Q10;
            {var subQ0=sQuery(id+"F0.wireOp",EDGE,"E7.top");var subQ1=sQuery(id+"F0.wireOp",EDGE,"E5.top");var subQ2=sQuery(id+"F0.wireOp",EDGE,"E0.top");var subQ3=sQuery(id+"F0.wireOp",EDGE,"E0.left");Q10=makeQuery(id+"F8.boolean.opBoolean","SPLIT",EDGE,{"disambiguationData":[TD([makeQuery(id+"F1.opExtrude","CAP_FACE",FACE,{"disambiguationData":[OSD([sQuery(id+"F0.wireOp",EDGE,"E0.bottom"),subQ2,subQ3,sQuery(id+"F0.wireOp",EDGE,"E0.right"),sQuery(id+"F0.wireOp",EDGE,"E1.3"),sQuery(id+"F0.wireOp",EDGE,"E3.top"),sQuery(id+"F0.wireOp",EDGE,"E3.left"),sQuery(id+"F0.wireOp",EDGE,"E3.right"),sQuery(id+"F0.wireOp",EDGE,"E5.bottom"),subQ1,sQuery(id+"F0.wireOp",EDGE,"E5.left"),sQuery(id+"F0.wireOp",EDGE,"E5.right"),subQ0,sQuery(id+"F0.wireOp",EDGE,"E7.left"),sQuery(id+"F0.wireOp",EDGE,"E7.right"),sQuery(id+"F0.wireOp",EDGE,"E9.trimOffspring"),sQuery(id+"F0.wireOp",EDGE,"E10.trimOffspring"),sQuery(id+"F0.wireOp",EDGE,"E11.trimOffspring"),sQuery(id+"F0.wireOp",EDGE,"E12.trimOffspring"),sQuery(id+"F0.wireOp",EDGE,"E13.trimOffspring"),sQuery(id+"F0.wireOp",EDGE,"E14.trimOffspring"),sQuery(id+"F0.wireOp",EDGE,"E15.trimOffspring"),sQuery(id+"F0.wireOp",EDGE,"E17.MirrorCS"),sQuery(id+"F0.wireOp",EDGE,"E18.MirrorCS"),sQuery(id+"F0.wireOp",EDGE,"E20.MirrorCS"),sQuery(id+"F0.wireOp",EDGE,"E21.MirrorCS"),sQuery(id+"F0.wireOp",EDGE,"E24.MirrorCS"),sQuery(id+"F0.wireOp",EDGE,"E25.MirrorCS"),sQuery(id+"F0.wireOp",EDGE,"E26.MirrorCS"),sQuery(id+"F0.wireOp",EDGE,"E27.MirrorCS"),sQuery(id+"F0.wireOp",EDGE,"E1.1"),sQuery(id+"F0.wireOp",EDGE,"E30"),sQuery(id+"F0.wireOp",EDGE,"E31"),sQuery(id+"F0.wireOp",EDGE,"E32"),sQuery(id+"F0.wireOp",EDGE,"E33"),sQuery(id+"F0.wireOp",EDGE,"E34"),sQuery(id+"F0.wireOp",EDGE,"E35")])],"isStart":false})])],"derivedFrom":makeQuery(id+"F2.boolean.opBoolean","MERGE",EDGE,{"derivedFrom":[makeQuery(id+"F1.opExtrude","SWEPT_EDGE",EDGE,{"disambiguationData":[OSD([subQ2,subQ3])]}),makeQuery(id+"F2.opExtrude","SWEPT_EDGE",EDGE,{"disambiguationData":[OSD([subQ2,subQ3])]})]})});}
            var Q11;
            {var subQ0=sQuery(id+"F0.wireOp",EDGE,"E12.trimOffspring");var subQ1=sQuery(id+"F0.wireOp",EDGE,"E5.bottom");var subQ2=sQuery(id+"F0.wireOp",EDGE,"E3.top");var subQ3=sQuery(id+"F0.wireOp",EDGE,"E0.bottom");var subQ4=sQuery(id+"F0.wireOp",EDGE,"E0.left");Q11=makeQuery(id+"F8.boolean.opBoolean","SPLIT",EDGE,{"disambiguationData":[TD([makeQuery(id+"F1.opExtrude","CAP_FACE",FACE,{"disambiguationData":[OSD([subQ3,sQuery(id+"F0.wireOp",EDGE,"E0.top"),subQ4,sQuery(id+"F0.wireOp",EDGE,"E0.right"),sQuery(id+"F0.wireOp",EDGE,"E1.3"),subQ2,sQuery(id+"F0.wireOp",EDGE,"E3.left"),sQuery(id+"F0.wireOp",EDGE,"E3.right"),subQ1,sQuery(id+"F0.wireOp",EDGE,"E5.top"),sQuery(id+"F0.wireOp",EDGE,"E5.left"),sQuery(id+"F0.wireOp",EDGE,"E5.right"),sQuery(id+"F0.wireOp",EDGE,"E7.top"),sQuery(id+"F0.wireOp",EDGE,"E7.left"),sQuery(id+"F0.wireOp",EDGE,"E7.right"),sQuery(id+"F0.wireOp",EDGE,"E9.trimOffspring"),sQuery(id+"F0.wireOp",EDGE,"E10.trimOffspring"),sQuery(id+"F0.wireOp",EDGE,"E11.trimOffspring"),subQ0,sQuery(id+"F0.wireOp",EDGE,"E13.trimOffspring"),sQuery(id+"F0.wireOp",EDGE,"E14.trimOffspring"),sQuery(id+"F0.wireOp",EDGE,"E15.trimOffspring"),sQuery(id+"F0.wireOp",EDGE,"E17.MirrorCS"),sQuery(id+"F0.wireOp",EDGE,"E18.MirrorCS"),sQuery(id+"F0.wireOp",EDGE,"E20.MirrorCS"),sQuery(id+"F0.wireOp",EDGE,"E21.MirrorCS"),sQuery(id+"F0.wireOp",EDGE,"E24.MirrorCS"),sQuery(id+"F0.wireOp",EDGE,"E25.MirrorCS"),sQuery(id+"F0.wireOp",EDGE,"E26.MirrorCS"),sQuery(id+"F0.wireOp",EDGE,"E27.MirrorCS"),sQuery(id+"F0.wireOp",EDGE,"E1.1"),sQuery(id+"F0.wireOp",EDGE,"E30"),sQuery(id+"F0.wireOp",EDGE,"E31"),sQuery(id+"F0.wireOp",EDGE,"E32"),sQuery(id+"F0.wireOp",EDGE,"E33"),sQuery(id+"F0.wireOp",EDGE,"E34"),sQuery(id+"F0.wireOp",EDGE,"E35")])],"isStart":false})])],"derivedFrom":makeQuery(id+"F2.boolean.opBoolean","MERGE",EDGE,{"derivedFrom":[makeQuery(id+"F1.opExtrude","SWEPT_EDGE",EDGE,{"disambiguationData":[OSD([subQ3,subQ4])]}),makeQuery(id+"F2.opExtrude","SWEPT_EDGE",EDGE,{"disambiguationData":[OSD([subQ3,subQ4])]})]})});}
            var Q12;
            Q12=makeQuery(id+"F8.boolean.opBoolean","COPY",EDGE,{"derivedFrom":makeQuery(id+"F8.opExtrude","CAP_EDGE",EDGE,{"disambiguationData":[OSD([sQuery(id+"F7.wireOp",EDGE,"E99.MirrorC")])],"isStart":true})});
            var Q13;
            {var subQ0=sQuery(id+"F0.wireOp",EDGE,"E0.left");Q13=makeQuery(id+"F8.boolean.opBoolean","INTERSECT",EDGE,{"derivedFrom":[makeQuery(id+"F2.boolean.opBoolean","MERGE",FACE,{"derivedFrom":[makeQuery(id+"F1.opExtrude","SWEPT_FACE",FACE,{"disambiguationData":[OSD([subQ0])]}),makeQuery(id+"F2.opExtrude","SWEPT_FACE",FACE,{"disambiguationData":[OSD([subQ0])]})]}),makeQuery(id+"F8.opExtrude","SWEPT_FACE",FACE,{"disambiguationData":[OSD([sQuery(id+"F7.wireOp",EDGE,"E98")])]})]});}
            var Q14;
            {var subQ0=sQuery(id+"F0.wireOp",EDGE,"E0.left");Q14=makeQuery(id+"F8.boolean.opBoolean","INTERSECT",EDGE,{"derivedFrom":[makeQuery(id+"F2.boolean.opBoolean","MERGE",FACE,{"derivedFrom":[makeQuery(id+"F1.opExtrude","SWEPT_FACE",FACE,{"disambiguationData":[OSD([subQ0])]}),makeQuery(id+"F2.opExtrude","SWEPT_FACE",FACE,{"disambiguationData":[OSD([subQ0])]})]}),makeQuery(id+"F8.opExtrude","SWEPT_FACE",FACE,{"disambiguationData":[OSD([sQuery(id+"F7.wireOp",EDGE,"E99.MirrorC")])]})]});}
            var Q15;
            Q15=makeQuery(id+"F1.opExtrude","CAP_EDGE",EDGE,{"disambiguationData":[OSD([sQuery(id+"F0.wireOp",EDGE,"E26.MirrorCS")])],"isStart":false});
            var Q16;
            Q16=makeQuery(id+"F1.opExtrude","CAP_EDGE",EDGE,{"disambiguationData":[OSD([sQuery(id+"F0.wireOp",EDGE,"E34")])],"isStart":false});
            var Q17;
            Q17=makeQuery(id+"F1.opExtrude","CAP_EDGE",EDGE,{"disambiguationData":[OSD([sQuery(id+"F0.wireOp",EDGE,"E27.MirrorCS")])],"isStart":false});
            var Q18;
            Q18=makeQuery(id+"F1.opExtrude","CAP_EDGE",EDGE,{"disambiguationData":[OSD([sQuery(id+"F0.wireOp",EDGE,"E1.1")])],"isStart":false});
            var Q19;
            Q19=makeQuery(id+"F1.opExtrude","CAP_EDGE",EDGE,{"disambiguationData":[OSD([sQuery(id+"F0.wireOp",EDGE,"E33")])],"isStart":false});
            var Q20;
            Q20=makeQuery(id+"F1.opExtrude","CAP_EDGE",EDGE,{"disambiguationData":[OSD([sQuery(id+"F0.wireOp",EDGE,"E24.MirrorCS")])],"isStart":false});
            var Q21;
            Q21=makeQuery(id+"F1.opExtrude","CAP_EDGE",EDGE,{"disambiguationData":[OSD([sQuery(id+"F0.wireOp",EDGE,"E25.MirrorCS")])],"isStart":false});
            var Q22;
            Q22=makeQuery(id+"F1.opExtrude","CAP_EDGE",EDGE,{"disambiguationData":[OSD([sQuery(id+"F0.wireOp",EDGE,"E35")])],"isStart":false});
            var Q23;
            Q23=makeQuery(id+"F1.opExtrude","CAP_EDGE",EDGE,{"disambiguationData":[OSD([sQuery(id+"F0.wireOp",EDGE,"E30")])],"isStart":false});
            var Q24;
            Q24=makeQuery(id+"F1.opExtrude","CAP_EDGE",EDGE,{"disambiguationData":[OSD([sQuery(id+"F0.wireOp",EDGE,"E20.MirrorCS")])],"isStart":false});
            var Q25;
            Q25=makeQuery(id+"F1.opExtrude","CAP_EDGE",EDGE,{"disambiguationData":[OSD([sQuery(id+"F0.wireOp",EDGE,"E21.MirrorCS")])],"isStart":false});
            var Q26;
            Q26=makeQuery(id+"F1.opExtrude","CAP_EDGE",EDGE,{"disambiguationData":[OSD([sQuery(id+"F0.wireOp",EDGE,"E31")])],"isStart":false});
            var Q27;
            Q27=makeQuery(id+"F1.opExtrude","CAP_EDGE",EDGE,{"disambiguationData":[OSD([sQuery(id+"F0.wireOp",EDGE,"E32")])],"isStart":false});
            var Q28;
            Q28=makeQuery(id+"F1.opExtrude","CAP_EDGE",EDGE,{"disambiguationData":[OSD([sQuery(id+"F0.wireOp",EDGE,"E17.MirrorCS")])],"isStart":false});
            var Q29;
            Q29=makeQuery(id+"F1.opExtrude","CAP_EDGE",EDGE,{"disambiguationData":[OSD([sQuery(id+"F0.wireOp",EDGE,"E18.MirrorCS")])],"isStart":false});
            var Q30;
            Q30=makeQuery(id+"F1.opExtrude","CAP_EDGE",EDGE,{"disambiguationData":[OSD([sQuery(id+"F0.wireOp",EDGE,"E3.left")])],"isStart":false});
            var Q31;
            Q31=makeQuery(id+"F1.opExtrude","CAP_EDGE",EDGE,{"disambiguationData":[OSD([sQuery(id+"F0.wireOp",EDGE,"E3.right")])],"isStart":false});
            var Q32;
            Q32=makeQuery(id+"F1.opExtrude","CAP_EDGE",EDGE,{"disambiguationData":[OSD([sQuery(id+"F0.wireOp",EDGE,"E15.trimOffspring")])],"isStart":false});
            var Q33;
            Q33=makeQuery(id+"F1.opExtrude","CAP_EDGE",EDGE,{"disambiguationData":[OSD([sQuery(id+"F0.wireOp",EDGE,"E5.left")])],"isStart":false});
            var Q34;
            Q34=makeQuery(id+"F1.opExtrude","CAP_EDGE",EDGE,{"disambiguationData":[OSD([sQuery(id+"F0.wireOp",EDGE,"E14.trimOffspring")])],"isStart":false});
            var Q35;
            Q35=makeQuery(id+"F1.opExtrude","CAP_EDGE",EDGE,{"disambiguationData":[OSD([sQuery(id+"F0.wireOp",EDGE,"E9.trimOffspring")])],"isStart":false});
            var Q36;
            Q36=makeQuery(id+"F1.opExtrude","CAP_EDGE",EDGE,{"disambiguationData":[OSD([sQuery(id+"F0.wireOp",EDGE,"E5.right")])],"isStart":false});
            var Q37;
            Q37=makeQuery(id+"F1.opExtrude","CAP_EDGE",EDGE,{"disambiguationData":[OSD([sQuery(id+"F0.wireOp",EDGE,"E13.trimOffspring")])],"isStart":false});
            var Q38;
            Q38=makeQuery(id+"F1.opExtrude","CAP_EDGE",EDGE,{"disambiguationData":[OSD([sQuery(id+"F0.wireOp",EDGE,"E10.trimOffspring")])],"isStart":false});
            var Q39;
            Q39=makeQuery(id+"F1.opExtrude","CAP_EDGE",EDGE,{"disambiguationData":[OSD([sQuery(id+"F0.wireOp",EDGE,"E1.3")])],"isStart":false});
            var Q40;
            Q40=makeQuery(id+"F1.opExtrude","CAP_EDGE",EDGE,{"disambiguationData":[OSD([sQuery(id+"F0.wireOp",EDGE,"E11.trimOffspring")])],"isStart":false});
            var Q41;
            Q41=makeQuery(id+"F1.opExtrude","CAP_EDGE",EDGE,{"disambiguationData":[OSD([sQuery(id+"F0.wireOp",EDGE,"E7.right")])],"isStart":false});
            var Q42;
            Q42=makeQuery(id+"F1.opExtrude","CAP_EDGE",EDGE,{"disambiguationData":[OSD([sQuery(id+"F0.wireOp",EDGE,"E7.left")])],"isStart":false});
            chamfer(context, id + "F9", {"entities" : qUnion([Q0, Q1, Q2, Q3, Q4, Q5, Q6, Q7, Q8, Q9, Q10, Q11, Q12, Q13, Q14, Q15, Q16, Q17, Q18, Q19, Q20, Q21, Q22, Q23, Q24, Q25, Q26, Q27, Q28, Q29, Q30, Q31, Q32, Q33, Q34, Q35, Q36, Q37, Q38, Q39, Q40, Q41, Q42]), "width" : 0.5 * mm, "tangentPropagation" : true});
        }
    });
